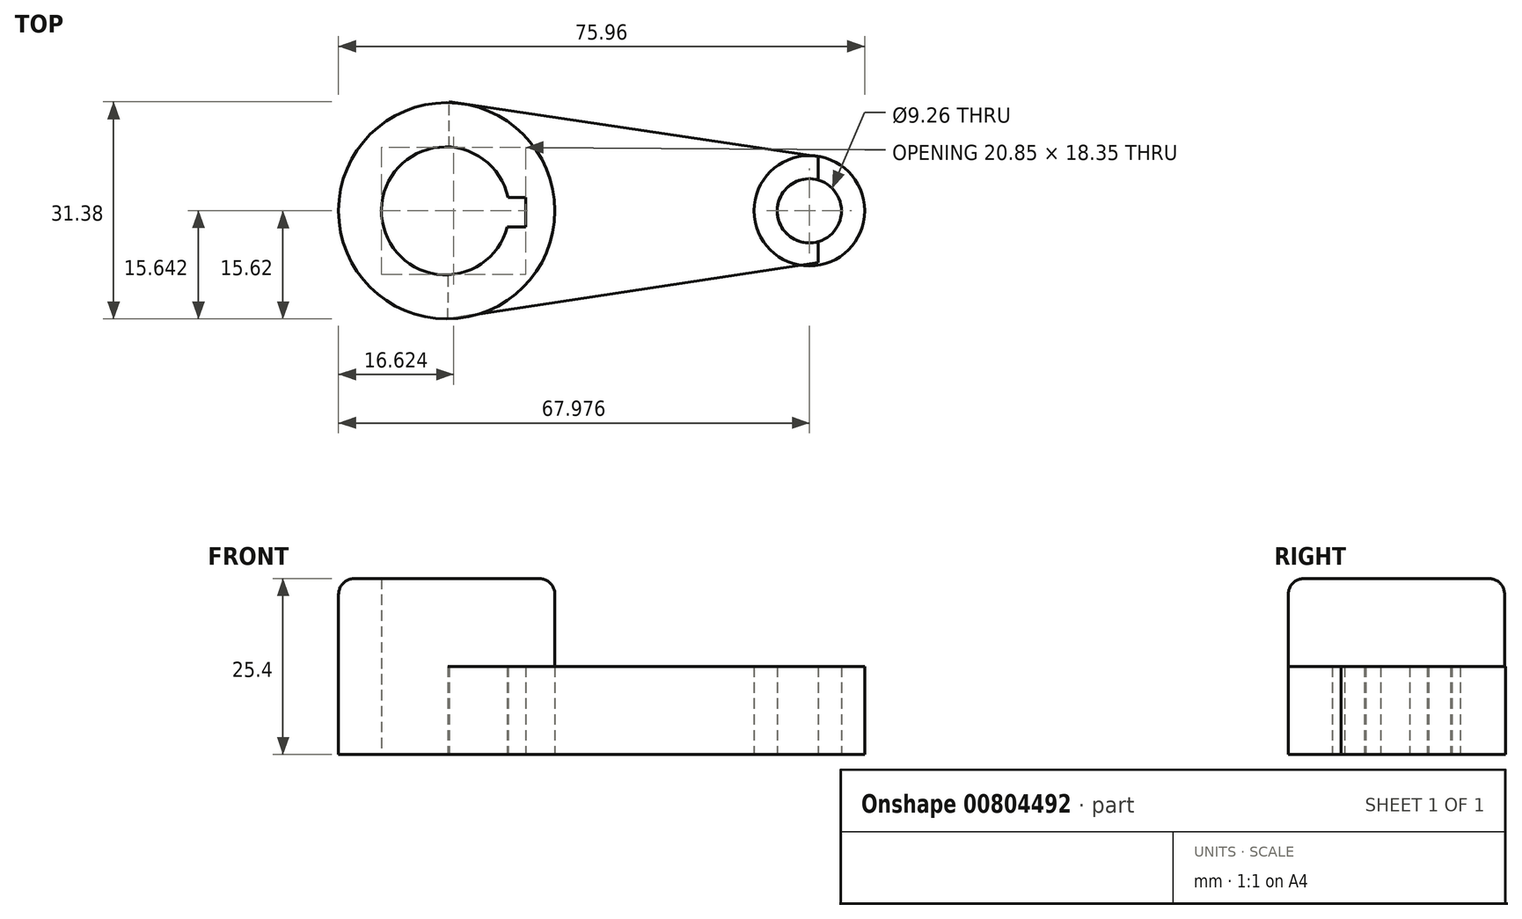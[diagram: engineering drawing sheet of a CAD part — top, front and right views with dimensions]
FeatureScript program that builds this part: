
annotation { "Feature Type Name" : "Feature", "Feature Type Description" : "" }
export const myFeature = defineFeature(function(context is Context, id is Id, definition is map)
    precondition{}
    {
        {
            var Q0;
            Q0=qCreatedBy(makeId("Top.planeOp"),FACE);
            var sketch = newSketch(context, id + "F0", { "sketchPlane" : qUnion([Q0])});
            skCircle(sketch, "E0", {"center": v(17.6, 0) * mm, "radius": 7.98 * mm});
            skCircle(sketch, "E1", {"center": v(-34.75, 0) * mm, "radius": 15.62 * mm});
            skSolve(sketch);
        }
        {
            var Q0;
            Q0=qCreatedBy(makeId("Top.planeOp"),FACE);
            var sketch = newSketch(context, id + "F1", { "sketchPlane" : qUnion([Q0])});
            skLineSegment(sketch, "E2", {"start": v(-34.38, 15.76) * mm, "end": v(18.9, 7.84) * mm});
            skLineSegment(sketch, "E3", {"start": v(18.9, 7.84) * mm, "end": v(18.9, -7.47) * mm});
            skLineSegment(sketch, "E4", {"start": v(18.9, -7.47) * mm, "end": v(-34.57, -15.58) * mm});
            skLineSegment(sketch, "E5", {"start": v(-34.57, -15.58) * mm, "end": v(-34.38, 15.76) * mm});
            skSolve(sketch);
        }
        {
            var Q0;
            Q0=makeQuery(id+"F0.imprint","IMPRINT",FACE,{"disambiguationData":[TD([[makeQuery(id+"F0.imprint","IMPRINT",EDGE,{"derivedFrom":sQuery(id+"F0.wireOp",EDGE,"E1")}),1.0]])]});
            extrude(context, id + "F2", {"entities" : qUnion([Q0]), "depth" : 25.4 * mm, "offsetDistance" : 25.4 * mm});
        }
        {
            var Q0;
            Q0=makeQuery(id+"F0.imprint","IMPRINT",FACE,{"disambiguationData":[TD([[makeQuery(id+"F0.imprint","IMPRINT",EDGE,{"derivedFrom":sQuery(id+"F0.wireOp",EDGE,"E0")}),1.0]])]});
            extrude(context, id + "F3", {"entities" : qUnion([Q0]), "depth" : 12.7 * mm, "offsetDistance" : 25.4 * mm});
        }
        {
            var Q0;
            Q0=makeQuery(id+"F1.imprint","IMPRINT",FACE,{"disambiguationData":[TD([[makeQuery(id+"F1.imprint","IMPRINT",EDGE,{"derivedFrom":sQuery(id+"F1.wireOp",EDGE,"E2")}),-1.0]])]});
            extrude(context, id + "F4", {"entities" : qUnion([Q0]), "depth" : 12.7 * mm, "offsetDistance" : 25.4 * mm});
        }
        {
            var Q0;
            Q0=qCreatedBy(makeId("Top.planeOp"),FACE);
            var sketch = newSketch(context, id + "F5", { "sketchPlane" : qUnion([Q0])});
            skCircle(sketch, "E6", {"center": v(17.6, 0) * mm, "radius": 4.63 * mm});
            skSolve(sketch);
        }
        {
            var Q0;
            Q0=qSketchRegion(id+"F5",true);
            extrude(context, id + "F6", {"entities" : qUnion([Q0]), "operationType" : NewBodyOperationType.REMOVE, "depth" : 12.7 * mm, "offsetDistance" : 25.4 * mm});
        }
        {
            var Q0;
            Q0=qCreatedBy(makeId("Top.planeOp"),FACE);
            var sketch = newSketch(context, id + "F7", { "sketchPlane" : qUnion([Q0])});
            skCircle(sketch, "E7", {"center": v(-34.94, 0) * mm, "radius": 9.24 * mm});
            skSolve(sketch);
        }
        {
            var Q0;
            Q0=qSketchRegion(id+"F7",true);
            extrude(context, id + "F8", {"entities" : qUnion([Q0]), "operationType" : NewBodyOperationType.REMOVE, "depth" : 25.4 * mm, "offsetDistance" : 25.4 * mm});
        }
        {
            var Q0;
            Q0=qCreatedBy(makeId("Top.planeOp"),FACE);
            var sketch = newSketch(context, id + "F9", { "sketchPlane" : qUnion([Q0])});
            skLineSegment(sketch, "E8.bottom", {"start": v(-28.67, 1.94) * mm, "end": v(-23.32, 1.94) * mm});
            skLineSegment(sketch, "E8.top", {"start": v(-28.67, -2.3) * mm, "end": v(-23.32, -2.3) * mm});
            skLineSegment(sketch, "E8.left", {"start": v(-28.67, 1.94) * mm, "end": v(-28.67, -2.3) * mm});
            skLineSegment(sketch, "E8.right", {"start": v(-23.32, 1.94) * mm, "end": v(-23.32, -2.3) * mm});
            skSolve(sketch);
        }
        {
            var Q0;
            Q0=qSketchRegion(id+"F9",true);
            extrude(context, id + "F10", {"entities" : qUnion([Q0]), "operationType" : NewBodyOperationType.REMOVE, "depth" : 25.4 * mm, "offsetDistance" : 25.4 * mm});
        }
        {
            var Q0;
            Q0=makeQuery(id+"F2.opExtrude","CAP_EDGE",EDGE,{"disambiguationData":[OSD([sQuery(id+"F0.wireOp",EDGE,"E1")])],"isStart":false});
            fillet(context, id + "F11", {"entities" : qUnion([Q0]), "radius" : 2.3 * mm, "tangentPropagation" : true, "allowEdgeOverflow" : false});
        }
    });
